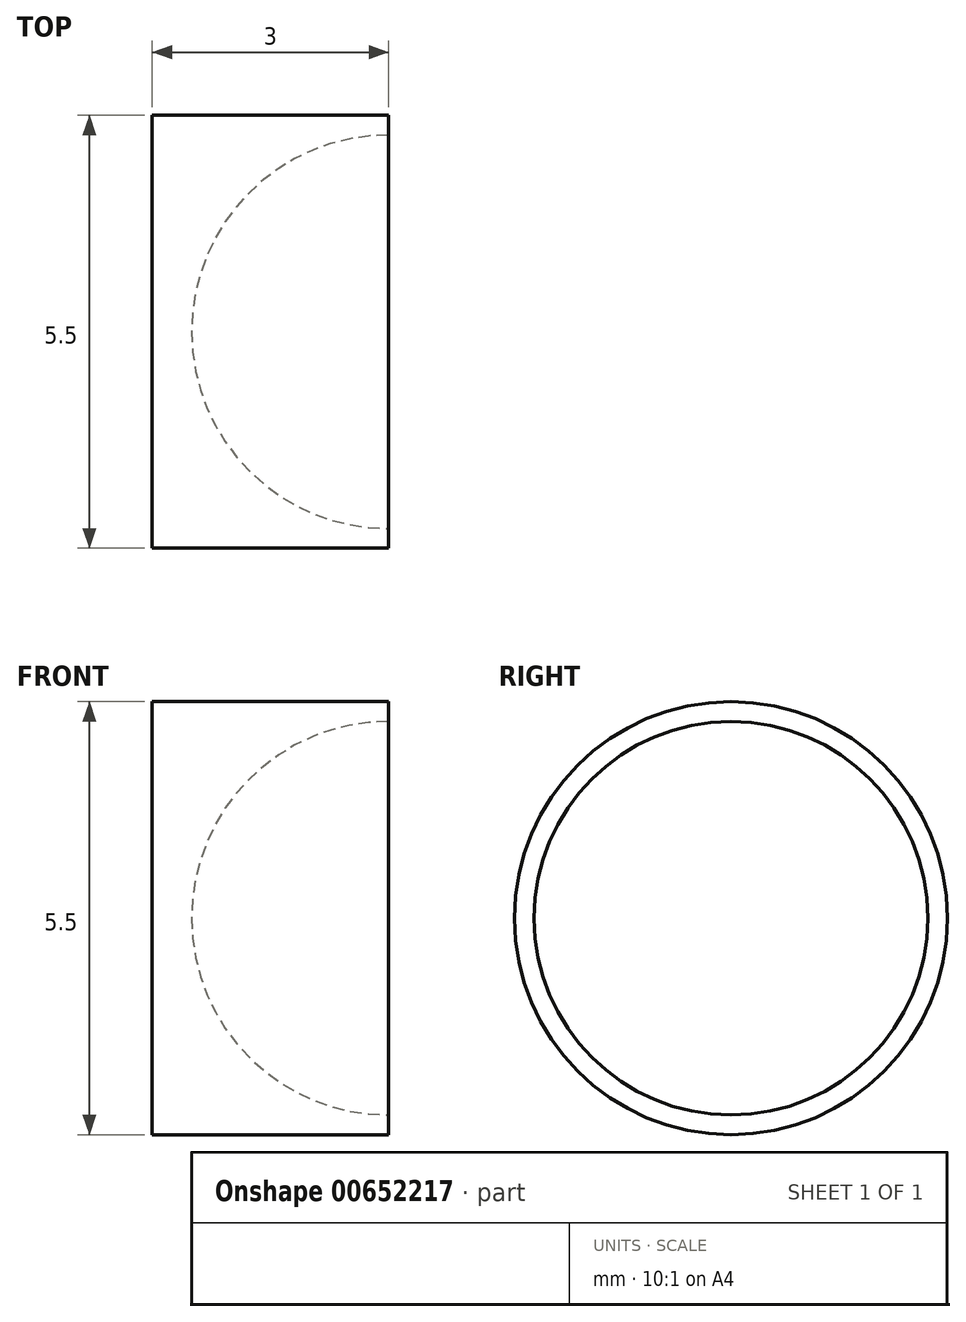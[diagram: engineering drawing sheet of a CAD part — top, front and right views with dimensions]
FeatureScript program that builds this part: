
annotation { "Feature Type Name" : "Feature", "Feature Type Description" : "" }
export const myFeature = defineFeature(function(context is Context, id is Id, definition is map)
    precondition{}
    {
        {
            var Q0;
            Q0=qCreatedBy(makeId("Right.planeOp"),FACE);
            var sketch = newSketch(context, id + "F0", { "sketchPlane" : qUnion([Q0])});
            skCircle(sketch, "E0", {"center": v(0, 0) * mm, "radius": 2.75 * mm});
            skSolve(sketch);
        }
        {
            var Q0;
            Q0=qSketchRegion(id+"F0",true);
            extrude(context, id + "F1", {"entities" : qUnion([Q0]), "depth" : 3 * mm, "offsetDistance" : 25 * mm});
        }
        {
            var Q0;
            Q0=qCreatedBy(makeId("Top.planeOp"),FACE);
            var sketch = newSketch(context, id + "F2", { "sketchPlane" : qUnion([Q0])});
            skArc(sketch, "E1", {"start": v(3, 2.5) * mm, "mid": v(0.5, 0) * mm, "end": v(3, -2.5) * mm});
            skLineSegment(sketch, "E2", {"start": v(3, 2.5) * mm, "end": v(3, -2.5) * mm});
            skSolve(sketch);
        }
        {
            var Q0;
            Q0=qSketchRegion(id+"F2",true);
            var Q1;
            Q1=sQuery(id+"F2.wireOp",EDGE,"E2");
            revolve(context, id + "F3", {"operationType" : NewBodyOperationType.REMOVE, "entities" : qUnion([Q0]), "axis" : qUnion([Q1]), "revolveType" : RevolveType.FULL, "oppositeDirection" : true});
        }
    });
